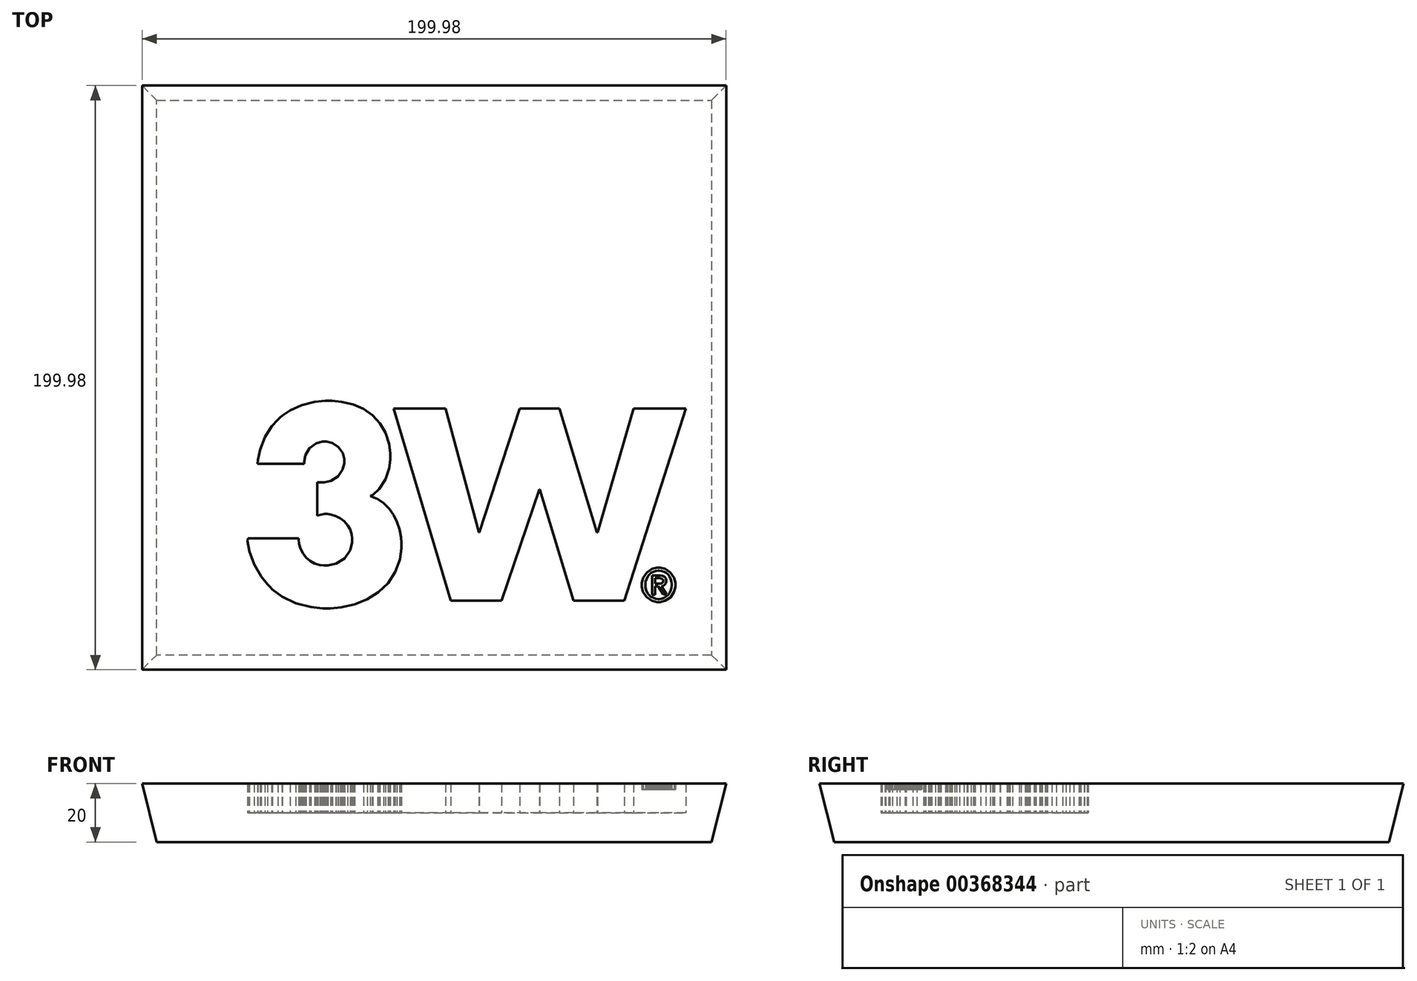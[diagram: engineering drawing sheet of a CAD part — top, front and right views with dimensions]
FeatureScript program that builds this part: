
annotation { "Feature Type Name" : "Feature", "Feature Type Description" : "" }
export const myFeature = defineFeature(function(context is Context, id is Id, definition is map)
    precondition{}
    {
        {
            var Q0;
            Q0=qCreatedBy(makeId("Top.planeOp"),FACE);
            var sketch = newSketch(context, id + "F0", { "sketchPlane" : qUnion([Q0])});
            skLineSegment(sketch, "E0", {"start": v(-100, 100) * mm, "end": v(100, 100) * mm});
            skLineSegment(sketch, "E1", {"start": v(100, 100) * mm, "end": v(100, -100) * mm});
            skLineSegment(sketch, "E2", {"start": v(100, -100) * mm, "end": v(-100, -100) * mm});
            skLineSegment(sketch, "E3", {"start": v(-100, -100) * mm, "end": v(-100, 100) * mm});
            skLineSegment(sketch, "E4", {"start": v(76.92, -70.57) * mm, "end": v(77.07, -70.57) * mm});
            skLineSegment(sketch, "E5", {"start": v(77.07, -70.57) * mm, "end": v(77.5, -70.55) * mm});
            skLineSegment(sketch, "E6", {"start": v(77.5, -70.55) * mm, "end": v(77.99, -70.42) * mm});
            skLineSegment(sketch, "E7", {"start": v(77.99, -70.42) * mm, "end": v(78.32, -70.11) * mm});
            skLineSegment(sketch, "E8", {"start": v(78.32, -70.11) * mm, "end": v(78.44, -69.69) * mm});
            skLineSegment(sketch, "E9", {"start": v(78.44, -69.69) * mm, "end": v(78.44, -69.55) * mm});
            skLineSegment(sketch, "E10", {"start": v(78.44, -69.55) * mm, "end": v(78.44, -69.43) * mm});
            skLineSegment(sketch, "E11", {"start": v(78.44, -69.43) * mm, "end": v(78.3, -69.08) * mm});
            skLineSegment(sketch, "E12", {"start": v(78.3, -69.08) * mm, "end": v(77.97, -68.82) * mm});
            skLineSegment(sketch, "E13", {"start": v(77.97, -68.82) * mm, "end": v(77.52, -68.7) * mm});
            skLineSegment(sketch, "E14", {"start": v(77.52, -68.7) * mm, "end": v(77.15, -68.67) * mm});
            skLineSegment(sketch, "E15", {"start": v(77.15, -68.67) * mm, "end": v(77.03, -68.67) * mm});
            skLineSegment(sketch, "E16", {"start": v(77.03, -68.67) * mm, "end": v(75.72, -68.67) * mm});
            skLineSegment(sketch, "E17", {"start": v(75.72, -68.67) * mm, "end": v(75.72, -70.57) * mm});
            skLineSegment(sketch, "E18", {"start": v(75.72, -70.57) * mm, "end": v(76.92, -70.57) * mm});
            skLineSegment(sketch, "E19", {"start": v(75.72, -74.28) * mm, "end": v(74.67, -74.28) * mm});
            skLineSegment(sketch, "E20", {"start": v(74.67, -74.28) * mm, "end": v(74.67, -67.75) * mm});
            skLineSegment(sketch, "E21", {"start": v(74.67, -67.75) * mm, "end": v(77.14, -67.75) * mm});
            skLineSegment(sketch, "E22", {"start": v(77.14, -67.75) * mm, "end": v(77.4, -67.75) * mm});
            skLineSegment(sketch, "E23", {"start": v(77.4, -67.75) * mm, "end": v(78.17, -67.86) * mm});
            skLineSegment(sketch, "E24", {"start": v(78.17, -67.86) * mm, "end": v(78.91, -68.2) * mm});
            skLineSegment(sketch, "E25", {"start": v(78.91, -68.2) * mm, "end": v(79.35, -68.78) * mm});
            skLineSegment(sketch, "E26", {"start": v(79.35, -68.78) * mm, "end": v(79.5, -69.4) * mm});
            skLineSegment(sketch, "E27", {"start": v(79.5, -69.4) * mm, "end": v(79.5, -69.62) * mm});
            skLineSegment(sketch, "E28", {"start": v(79.5, -69.62) * mm, "end": v(79.5, -69.8) * mm});
            skLineSegment(sketch, "E29", {"start": v(79.5, -69.8) * mm, "end": v(79.37, -70.37) * mm});
            skLineSegment(sketch, "E30", {"start": v(79.37, -70.37) * mm, "end": v(79, -70.9) * mm});
            skLineSegment(sketch, "E31", {"start": v(79, -70.9) * mm, "end": v(78.47, -71.23) * mm});
            skLineSegment(sketch, "E32", {"start": v(78.47, -71.23) * mm, "end": v(77.97, -71.36) * mm});
            skLineSegment(sketch, "E33", {"start": v(77.97, -71.36) * mm, "end": v(77.8, -71.38) * mm});
            skLineSegment(sketch, "E34", {"start": v(77.8, -71.38) * mm, "end": v(79.64, -74.24) * mm});
            skLineSegment(sketch, "E35", {"start": v(79.64, -74.24) * mm, "end": v(78.44, -74.24) * mm});
            skLineSegment(sketch, "E36", {"start": v(78.44, -74.24) * mm, "end": v(76.75, -71.46) * mm});
            skLineSegment(sketch, "E37", {"start": v(76.75, -71.46) * mm, "end": v(75.72, -71.46) * mm});
            skLineSegment(sketch, "E38", {"start": v(75.72, -71.46) * mm, "end": v(75.72, -74.28) * mm});
            skLineSegment(sketch, "E39", {"start": v(76.89, -66.06) * mm, "end": v(76.66, -66.06) * mm});
            skLineSegment(sketch, "E40", {"start": v(76.66, -66.06) * mm, "end": v(75.96, -66.15) * mm});
            skLineSegment(sketch, "E41", {"start": v(75.96, -66.15) * mm, "end": v(75.1, -66.42) * mm});
            skLineSegment(sketch, "E42", {"start": v(75.1, -66.42) * mm, "end": v(74.33, -66.84) * mm});
            skLineSegment(sketch, "E43", {"start": v(74.33, -66.84) * mm, "end": v(73.66, -67.42) * mm});
            skLineSegment(sketch, "E44", {"start": v(73.66, -67.42) * mm, "end": v(73.1, -68.13) * mm});
            skLineSegment(sketch, "E45", {"start": v(73.1, -68.13) * mm, "end": v(72.7, -68.96) * mm});
            skLineSegment(sketch, "E46", {"start": v(72.7, -68.96) * mm, "end": v(72.43, -69.9) * mm});
            skLineSegment(sketch, "E47", {"start": v(72.43, -69.9) * mm, "end": v(72.34, -70.67) * mm});
            skLineSegment(sketch, "E48", {"start": v(72.34, -70.67) * mm, "end": v(72.34, -70.93) * mm});
            skLineSegment(sketch, "E49", {"start": v(72.34, -70.93) * mm, "end": v(72.34, -71.17) * mm});
            skLineSegment(sketch, "E50", {"start": v(72.34, -71.17) * mm, "end": v(72.42, -71.9) * mm});
            skLineSegment(sketch, "E51", {"start": v(72.42, -71.9) * mm, "end": v(72.65, -72.82) * mm});
            skLineSegment(sketch, "E52", {"start": v(72.65, -72.82) * mm, "end": v(73.03, -73.64) * mm});
            skLineSegment(sketch, "E53", {"start": v(73.03, -73.64) * mm, "end": v(73.55, -74.36) * mm});
            skLineSegment(sketch, "E54", {"start": v(73.55, -74.36) * mm, "end": v(74.2, -74.96) * mm});
            skLineSegment(sketch, "E55", {"start": v(74.2, -74.96) * mm, "end": v(74.99, -75.4) * mm});
            skLineSegment(sketch, "E56", {"start": v(74.99, -75.4) * mm, "end": v(75.88, -75.7) * mm});
            skLineSegment(sketch, "E57", {"start": v(75.88, -75.7) * mm, "end": v(76.64, -75.8) * mm});
            skLineSegment(sketch, "E58", {"start": v(76.64, -75.8) * mm, "end": v(76.89, -75.8) * mm});
            skLineSegment(sketch, "E59", {"start": v(76.89, -75.8) * mm, "end": v(77.12, -75.8) * mm});
            skLineSegment(sketch, "E60", {"start": v(77.12, -75.8) * mm, "end": v(77.8, -75.7) * mm});
            skLineSegment(sketch, "E61", {"start": v(77.8, -75.7) * mm, "end": v(78.65, -75.44) * mm});
            skLineSegment(sketch, "E62", {"start": v(78.65, -75.44) * mm, "end": v(79.42, -75.01) * mm});
            skLineSegment(sketch, "E63", {"start": v(79.42, -75.01) * mm, "end": v(80.08, -74.44) * mm});
            skLineSegment(sketch, "E64", {"start": v(80.08, -74.44) * mm, "end": v(80.63, -73.74) * mm});
            skLineSegment(sketch, "E65", {"start": v(80.63, -73.74) * mm, "end": v(81.05, -72.9) * mm});
            skLineSegment(sketch, "E66", {"start": v(81.05, -72.9) * mm, "end": v(81.31, -71.97) * mm});
            skLineSegment(sketch, "E67", {"start": v(81.31, -71.97) * mm, "end": v(81.4, -71.19) * mm});
            skLineSegment(sketch, "E68", {"start": v(81.4, -71.19) * mm, "end": v(81.4, -70.93) * mm});
            skLineSegment(sketch, "E69", {"start": v(81.4, -70.93) * mm, "end": v(81.4, -70.67) * mm});
            skLineSegment(sketch, "E70", {"start": v(81.4, -70.67) * mm, "end": v(81.31, -69.89) * mm});
            skLineSegment(sketch, "E71", {"start": v(81.31, -69.89) * mm, "end": v(81.05, -68.94) * mm});
            skLineSegment(sketch, "E72", {"start": v(81.05, -68.94) * mm, "end": v(80.64, -68.11) * mm});
            skLineSegment(sketch, "E73", {"start": v(80.64, -68.11) * mm, "end": v(80.1, -67.4) * mm});
            skLineSegment(sketch, "E74", {"start": v(80.1, -67.4) * mm, "end": v(79.43, -66.83) * mm});
            skLineSegment(sketch, "E75", {"start": v(79.43, -66.83) * mm, "end": v(78.66, -66.41) * mm});
            skLineSegment(sketch, "E76", {"start": v(78.66, -66.41) * mm, "end": v(77.81, -66.15) * mm});
            skLineSegment(sketch, "E77", {"start": v(77.81, -66.15) * mm, "end": v(77.12, -66.06) * mm});
            skLineSegment(sketch, "E78", {"start": v(77.12, -66.06) * mm, "end": v(76.89, -66.06) * mm});
            skLineSegment(sketch, "E79", {"start": v(76.89, -76.82) * mm, "end": v(76.3, -76.82) * mm});
            skLineSegment(sketch, "E80", {"start": v(76.3, -76.82) * mm, "end": v(74.55, -76.37) * mm});
            skLineSegment(sketch, "E81", {"start": v(74.55, -76.37) * mm, "end": v(72.72, -75.13) * mm});
            skLineSegment(sketch, "E82", {"start": v(72.72, -75.13) * mm, "end": v(71.53, -73.26) * mm});
            skLineSegment(sketch, "E83", {"start": v(71.53, -73.26) * mm, "end": v(71.1, -71.5) * mm});
            skLineSegment(sketch, "E84", {"start": v(71.1, -71.5) * mm, "end": v(71.1, -70.93) * mm});
            skLineSegment(sketch, "E85", {"start": v(71.1, -70.93) * mm, "end": v(71.1, -70.32) * mm});
            skLineSegment(sketch, "E86", {"start": v(71.1, -70.32) * mm, "end": v(71.57, -68.52) * mm});
            skLineSegment(sketch, "E87", {"start": v(71.57, -68.52) * mm, "end": v(72.83, -66.66) * mm});
            skLineSegment(sketch, "E88", {"start": v(72.83, -66.66) * mm, "end": v(74.67, -65.46) * mm});
            skLineSegment(sketch, "E89", {"start": v(74.67, -65.46) * mm, "end": v(76.33, -65.03) * mm});
            skLineSegment(sketch, "E90", {"start": v(76.33, -65.03) * mm, "end": v(76.89, -65.03) * mm});
            skLineSegment(sketch, "E91", {"start": v(76.89, -65.03) * mm, "end": v(77.44, -65.03) * mm});
            skLineSegment(sketch, "E92", {"start": v(77.44, -65.03) * mm, "end": v(79.1, -65.46) * mm});
            skLineSegment(sketch, "E93", {"start": v(79.1, -65.46) * mm, "end": v(80.93, -66.66) * mm});
            skLineSegment(sketch, "E94", {"start": v(80.93, -66.66) * mm, "end": v(82.18, -68.52) * mm});
            skLineSegment(sketch, "E95", {"start": v(82.18, -68.52) * mm, "end": v(82.64, -70.32) * mm});
            skLineSegment(sketch, "E96", {"start": v(82.64, -70.32) * mm, "end": v(82.64, -70.93) * mm});
            skLineSegment(sketch, "E97", {"start": v(82.64, -70.93) * mm, "end": v(82.64, -71.53) * mm});
            skLineSegment(sketch, "E98", {"start": v(82.64, -71.53) * mm, "end": v(82.2, -73.33) * mm});
            skLineSegment(sketch, "E99", {"start": v(82.2, -73.33) * mm, "end": v(80.94, -75.2) * mm});
            skLineSegment(sketch, "E100", {"start": v(80.94, -75.2) * mm, "end": v(79.1, -76.4) * mm});
            skLineSegment(sketch, "E101", {"start": v(79.1, -76.4) * mm, "end": v(77.44, -76.82) * mm});
            skLineSegment(sketch, "E102", {"start": v(77.44, -76.82) * mm, "end": v(76.89, -76.82) * mm});
            skLineSegment(sketch, "E103", {"start": v(-60.45, -29.5) * mm, "end": v(-60.32, -28.28) * mm});
            skLineSegment(sketch, "E104", {"start": v(-60.32, -28.28) * mm, "end": v(-59.54, -24.65) * mm});
            skLineSegment(sketch, "E105", {"start": v(-59.54, -24.65) * mm, "end": v(-57.91, -20.4) * mm});
            skLineSegment(sketch, "E106", {"start": v(-57.91, -20.4) * mm, "end": v(-55.63, -16.72) * mm});
            skLineSegment(sketch, "E107", {"start": v(-55.63, -16.72) * mm, "end": v(-53.54, -14.33) * mm});
            skLineSegment(sketch, "E108", {"start": v(-53.54, -14.33) * mm, "end": v(-52.76, -13.63) * mm});
            skLineSegment(sketch, "E109", {"start": v(-52.76, -13.63) * mm, "end": v(-51.97, -12.93) * mm});
            skLineSegment(sketch, "E110", {"start": v(-51.97, -12.93) * mm, "end": v(-49.32, -11.17) * mm});
            skLineSegment(sketch, "E111", {"start": v(-49.32, -11.17) * mm, "end": v(-45.33, -9.4) * mm});
            skLineSegment(sketch, "E112", {"start": v(-45.33, -9.4) * mm, "end": v(-40.87, -8.32) * mm});
            skLineSegment(sketch, "E113", {"start": v(-40.87, -8.32) * mm, "end": v(-37.22, -7.96) * mm});
            skLineSegment(sketch, "E114", {"start": v(-37.22, -7.96) * mm, "end": v(-36, -7.96) * mm});
            skLineSegment(sketch, "E115", {"start": v(-36, -7.96) * mm, "end": v(-34.93, -7.96) * mm});
            skLineSegment(sketch, "E116", {"start": v(-34.93, -7.96) * mm, "end": v(-31.72, -8.27) * mm});
            skLineSegment(sketch, "E117", {"start": v(-31.72, -8.27) * mm, "end": v(-27.75, -9.21) * mm});
            skLineSegment(sketch, "E118", {"start": v(-27.75, -9.21) * mm, "end": v(-24.17, -10.76) * mm});
            skLineSegment(sketch, "E119", {"start": v(-24.17, -10.76) * mm, "end": v(-21.07, -12.9) * mm});
            skLineSegment(sketch, "E120", {"start": v(-21.07, -12.9) * mm, "end": v(-18.52, -15.61) * mm});
            skLineSegment(sketch, "E121", {"start": v(-18.52, -15.61) * mm, "end": v(-16.6, -18.9) * mm});
            skLineSegment(sketch, "E122", {"start": v(-16.6, -18.9) * mm, "end": v(-15.4, -22.72) * mm});
            skLineSegment(sketch, "E123", {"start": v(-15.4, -22.72) * mm, "end": v(-14.98, -25.99) * mm});
            skLineSegment(sketch, "E124", {"start": v(-14.98, -25.99) * mm, "end": v(-14.98, -27.08) * mm});
            skLineSegment(sketch, "E125", {"start": v(-14.98, -27.08) * mm, "end": v(-14.98, -28.06) * mm});
            skLineSegment(sketch, "E126", {"start": v(-14.98, -28.06) * mm, "end": v(-15.38, -31.01) * mm});
            skLineSegment(sketch, "E127", {"start": v(-15.38, -31.01) * mm, "end": v(-16.62, -34.78) * mm});
            skLineSegment(sketch, "E128", {"start": v(-16.62, -34.78) * mm, "end": v(-18.76, -38.08) * mm});
            skLineSegment(sketch, "E129", {"start": v(-18.76, -38.08) * mm, "end": v(-21, -40.1) * mm});
            skLineSegment(sketch, "E130", {"start": v(-21, -40.1) * mm, "end": v(-21.85, -40.59) * mm});
            skLineSegment(sketch, "E131", {"start": v(-21.85, -40.59) * mm, "end": v(-21.22, -40.75) * mm});
            skLineSegment(sketch, "E132", {"start": v(-21.22, -40.75) * mm, "end": v(-19.39, -41.55) * mm});
            skLineSegment(sketch, "E133", {"start": v(-19.39, -41.55) * mm, "end": v(-17.23, -43) * mm});
            skLineSegment(sketch, "E134", {"start": v(-17.23, -43) * mm, "end": v(-15.4, -44.86) * mm});
            skLineSegment(sketch, "E135", {"start": v(-15.4, -44.86) * mm, "end": v(-13.87, -47.04) * mm});
            skLineSegment(sketch, "E136", {"start": v(-13.87, -47.04) * mm, "end": v(-12.68, -49.44) * mm});
            skLineSegment(sketch, "E137", {"start": v(-12.68, -49.44) * mm, "end": v(-11.82, -52) * mm});
            skLineSegment(sketch, "E138", {"start": v(-11.82, -52) * mm, "end": v(-11.3, -54.6) * mm});
            skLineSegment(sketch, "E139", {"start": v(-11.3, -54.6) * mm, "end": v(-11.13, -56.52) * mm});
            skLineSegment(sketch, "E140", {"start": v(-11.13, -56.52) * mm, "end": v(-11.13, -57.17) * mm});
            skLineSegment(sketch, "E141", {"start": v(-11.13, -57.17) * mm, "end": v(-11.13, -58.43) * mm});
            skLineSegment(sketch, "E142", {"start": v(-11.13, -58.43) * mm, "end": v(-11.7, -62.24) * mm});
            skLineSegment(sketch, "E143", {"start": v(-11.7, -62.24) * mm, "end": v(-13.29, -66.64) * mm});
            skLineSegment(sketch, "E144", {"start": v(-13.29, -66.64) * mm, "end": v(-15.77, -70.4) * mm});
            skLineSegment(sketch, "E145", {"start": v(-15.77, -70.4) * mm, "end": v(-19.01, -73.46) * mm});
            skLineSegment(sketch, "E146", {"start": v(-19.01, -73.46) * mm, "end": v(-22.86, -75.87) * mm});
            skLineSegment(sketch, "E147", {"start": v(-22.86, -75.87) * mm, "end": v(-27.19, -77.58) * mm});
            skLineSegment(sketch, "E148", {"start": v(-27.19, -77.58) * mm, "end": v(-31.85, -78.62) * mm});
            skLineSegment(sketch, "E149", {"start": v(-31.85, -78.62) * mm, "end": v(-35.5, -78.97) * mm});
            skLineSegment(sketch, "E150", {"start": v(-35.5, -78.97) * mm, "end": v(-36.7, -78.97) * mm});
            skLineSegment(sketch, "E151", {"start": v(-36.7, -78.97) * mm, "end": v(-38.08, -78.97) * mm});
            skLineSegment(sketch, "E152", {"start": v(-38.08, -78.97) * mm, "end": v(-42.2, -78.57) * mm});
            skLineSegment(sketch, "E153", {"start": v(-42.2, -78.57) * mm, "end": v(-47.35, -77.29) * mm});
            skLineSegment(sketch, "E154", {"start": v(-47.35, -77.29) * mm, "end": v(-52.08, -75) * mm});
            skLineSegment(sketch, "E155", {"start": v(-52.08, -75) * mm, "end": v(-55.37, -72.53) * mm});
            skLineSegment(sketch, "E156", {"start": v(-55.37, -72.53) * mm, "end": v(-56.32, -71.56) * mm});
            skLineSegment(sketch, "E157", {"start": v(-56.32, -71.56) * mm, "end": v(-57.1, -70.76) * mm});
            skLineSegment(sketch, "E158", {"start": v(-57.1, -70.76) * mm, "end": v(-59.17, -68.08) * mm});
            skLineSegment(sketch, "E159", {"start": v(-59.17, -68.08) * mm, "end": v(-61.61, -63.92) * mm});
            skLineSegment(sketch, "E160", {"start": v(-61.61, -63.92) * mm, "end": v(-63.29, -59.43) * mm});
            skLineSegment(sketch, "E161", {"start": v(-63.29, -59.43) * mm, "end": v(-63.87, -56.09) * mm});
            skLineSegment(sketch, "E162", {"start": v(-63.87, -56.09) * mm, "end": v(-63.83, -54.98) * mm});
            skLineSegment(sketch, "E163", {"start": v(-63.83, -54.98) * mm, "end": v(-46.37, -54.98) * mm});
            skLineSegment(sketch, "E164", {"start": v(-46.37, -54.98) * mm, "end": v(-46.37, -55.45) * mm});
            skLineSegment(sketch, "E165", {"start": v(-46.37, -55.45) * mm, "end": v(-46.2, -56.88) * mm});
            skLineSegment(sketch, "E166", {"start": v(-46.2, -56.88) * mm, "end": v(-45.7, -58.64) * mm});
            skLineSegment(sketch, "E167", {"start": v(-45.7, -58.64) * mm, "end": v(-44.9, -60.23) * mm});
            skLineSegment(sketch, "E168", {"start": v(-44.9, -60.23) * mm, "end": v(-43.82, -61.61) * mm});
            skLineSegment(sketch, "E169", {"start": v(-43.82, -61.61) * mm, "end": v(-42.5, -62.75) * mm});
            skLineSegment(sketch, "E170", {"start": v(-42.5, -62.75) * mm, "end": v(-40.93, -63.6) * mm});
            skLineSegment(sketch, "E171", {"start": v(-40.93, -63.6) * mm, "end": v(-39.15, -64.14) * mm});
            skLineSegment(sketch, "E172", {"start": v(-39.15, -64.14) * mm, "end": v(-37.69, -64.33) * mm});
            skLineSegment(sketch, "E173", {"start": v(-37.69, -64.33) * mm, "end": v(-37.2, -64.33) * mm});
            skLineSegment(sketch, "E174", {"start": v(-37.2, -64.33) * mm, "end": v(-36.3, -64.33) * mm});
            skLineSegment(sketch, "E175", {"start": v(-36.3, -64.33) * mm, "end": v(-33.56, -63.7) * mm});
            skLineSegment(sketch, "E176", {"start": v(-33.56, -63.7) * mm, "end": v(-30.66, -61.92) * mm});
            skLineSegment(sketch, "E177", {"start": v(-30.66, -61.92) * mm, "end": v(-28.73, -59.13) * mm});
            skLineSegment(sketch, "E178", {"start": v(-28.73, -59.13) * mm, "end": v(-28.03, -56.41) * mm});
            skLineSegment(sketch, "E179", {"start": v(-28.03, -56.41) * mm, "end": v(-28.03, -55.5) * mm});
            skLineSegment(sketch, "E180", {"start": v(-28.03, -55.5) * mm, "end": v(-28.03, -55.06) * mm});
            skLineSegment(sketch, "E181", {"start": v(-28.03, -55.06) * mm, "end": v(-28.22, -53.7) * mm});
            skLineSegment(sketch, "E182", {"start": v(-28.22, -53.7) * mm, "end": v(-28.77, -52.03) * mm});
            skLineSegment(sketch, "E183", {"start": v(-28.77, -52.03) * mm, "end": v(-29.63, -50.53) * mm});
            skLineSegment(sketch, "E184", {"start": v(-29.63, -50.53) * mm, "end": v(-30.76, -49.23) * mm});
            skLineSegment(sketch, "E185", {"start": v(-30.76, -49.23) * mm, "end": v(-32.12, -48.17) * mm});
            skLineSegment(sketch, "E186", {"start": v(-32.12, -48.17) * mm, "end": v(-33.65, -47.37) * mm});
            skLineSegment(sketch, "E187", {"start": v(-33.65, -47.37) * mm, "end": v(-35.33, -46.86) * mm});
            skLineSegment(sketch, "E188", {"start": v(-35.33, -46.86) * mm, "end": v(-36.65, -46.69) * mm});
            skLineSegment(sketch, "E189", {"start": v(-36.65, -46.69) * mm, "end": v(-37.1, -46.69) * mm});
            skLineSegment(sketch, "E190", {"start": v(-37.1, -46.69) * mm, "end": v(-37.47, -46.69) * mm});
            skLineSegment(sketch, "E191", {"start": v(-37.47, -46.69) * mm, "end": v(-38.62, -46.85) * mm});
            skLineSegment(sketch, "E192", {"start": v(-38.62, -46.85) * mm, "end": v(-39.82, -47.15) * mm});
            skLineSegment(sketch, "E193", {"start": v(-39.82, -47.15) * mm, "end": v(-40.06, -47.22) * mm});
            skLineSegment(sketch, "E194", {"start": v(-40.06, -47.22) * mm, "end": v(-40.06, -35.79) * mm});
            skLineSegment(sketch, "E195", {"start": v(-40.06, -35.79) * mm, "end": v(-38.33, -35.79) * mm});
            skLineSegment(sketch, "E196", {"start": v(-38.33, -35.79) * mm, "end": v(-37.57, -35.79) * mm});
            skLineSegment(sketch, "E197", {"start": v(-37.57, -35.79) * mm, "end": v(-35.3, -35.3) * mm});
            skLineSegment(sketch, "E198", {"start": v(-35.3, -35.3) * mm, "end": v(-32.93, -33.87) * mm});
            skLineSegment(sketch, "E199", {"start": v(-32.93, -33.87) * mm, "end": v(-31.37, -31.6) * mm});
            skLineSegment(sketch, "E200", {"start": v(-31.37, -31.6) * mm, "end": v(-30.81, -29.31) * mm});
            skLineSegment(sketch, "E201", {"start": v(-30.81, -29.31) * mm, "end": v(-30.81, -28.56) * mm});
            skLineSegment(sketch, "E202", {"start": v(-30.81, -28.56) * mm, "end": v(-30.81, -27.87) * mm});
            skLineSegment(sketch, "E203", {"start": v(-30.81, -27.87) * mm, "end": v(-31.33, -25.82) * mm});
            skLineSegment(sketch, "E204", {"start": v(-31.33, -25.82) * mm, "end": v(-32.74, -23.73) * mm});
            skLineSegment(sketch, "E205", {"start": v(-32.74, -23.73) * mm, "end": v(-34.86, -22.4) * mm});
            skLineSegment(sketch, "E206", {"start": v(-34.86, -22.4) * mm, "end": v(-36.85, -21.92) * mm});
            skLineSegment(sketch, "E207", {"start": v(-36.85, -21.92) * mm, "end": v(-37.52, -21.92) * mm});
            skLineSegment(sketch, "E208", {"start": v(-37.52, -21.92) * mm, "end": v(-38.25, -21.92) * mm});
            skLineSegment(sketch, "E209", {"start": v(-38.25, -21.92) * mm, "end": v(-40.46, -22.5) * mm});
            skLineSegment(sketch, "E210", {"start": v(-40.46, -22.5) * mm, "end": v(-42.68, -24.12) * mm});
            skLineSegment(sketch, "E211", {"start": v(-42.68, -24.12) * mm, "end": v(-44.06, -26.52) * mm});
            skLineSegment(sketch, "E212", {"start": v(-44.06, -26.52) * mm, "end": v(-44.51, -28.76) * mm});
            skLineSegment(sketch, "E213", {"start": v(-44.51, -28.76) * mm, "end": v(-44.5, -29.5) * mm});
            skLineSegment(sketch, "E214", {"start": v(-44.5, -29.5) * mm, "end": v(-60.45, -29.5) * mm});
            skLineSegment(sketch, "E215", {"start": v(15.33, -53.04) * mm, "end": v(15.5, -53.04) * mm});
            skLineSegment(sketch, "E216", {"start": v(15.5, -53.04) * mm, "end": v(29.3, -10.57) * mm});
            skLineSegment(sketch, "E217", {"start": v(29.3, -10.57) * mm, "end": v(42.88, -10.57) * mm});
            skLineSegment(sketch, "E218", {"start": v(42.88, -10.57) * mm, "end": v(55.8, -53.04) * mm});
            skLineSegment(sketch, "E219", {"start": v(55.8, -53.04) * mm, "end": v(55.97, -53.04) * mm});
            skLineSegment(sketch, "E220", {"start": v(55.97, -53.04) * mm, "end": v(68.35, -10.57) * mm});
            skLineSegment(sketch, "E221", {"start": v(68.35, -10.57) * mm, "end": v(86.17, -10.57) * mm});
            skLineSegment(sketch, "E222", {"start": v(86.17, -10.57) * mm, "end": v(65.14, -76.36) * mm});
            skLineSegment(sketch, "E223", {"start": v(65.14, -76.36) * mm, "end": v(47.68, -76.36) * mm});
            skLineSegment(sketch, "E224", {"start": v(47.68, -76.36) * mm, "end": v(36.18, -38.22) * mm});
            skLineSegment(sketch, "E225", {"start": v(36.18, -38.22) * mm, "end": v(36, -38.22) * mm});
            skLineSegment(sketch, "E226", {"start": v(36, -38.22) * mm, "end": v(23.09, -76.36) * mm});
            skLineSegment(sketch, "E227", {"start": v(23.09, -76.36) * mm, "end": v(5.73, -76.36) * mm});
            skLineSegment(sketch, "E228", {"start": v(5.73, -76.36) * mm, "end": v(-13.92, -10.57) * mm});
            skLineSegment(sketch, "E229", {"start": v(-13.92, -10.57) * mm, "end": v(3.9, -10.57) * mm});
            skLineSegment(sketch, "E230", {"start": v(3.9, -10.57) * mm, "end": v(15.33, -53.04) * mm});
            skSolve(sketch);
        }
        {
            var Q0;
            {var subQ4=sQuery(id+"F0.wireOp",EDGE,"E2");Q0=makeQuery(id+"F0.imprint","IMPRINT",FACE,{"disambiguationData":[TD([[makeQuery(id+"F0.imprint","IMPRINT",EDGE,{"derivedFrom":subQ4}),-1.0]])]});}
            var Q1;
            Q1=makeQuery(id+"F0.imprint","IMPRINT",FACE,{"disambiguationData":[TD([[makeQuery(id+"F0.imprint","IMPRINT",EDGE,{"derivedFrom":sQuery(id+"F0.wireOp",EDGE,"E19")}),1.0]])]});
            var Q2;
            Q2=makeQuery(id+"F0.imprint","IMPRINT",FACE,{"disambiguationData":[TD([[makeQuery(id+"F0.imprint","IMPRINT",EDGE,{"derivedFrom":sQuery(id+"F0.wireOp",EDGE,"E4")}),1.0]])]});
            extrude(context, id + "F1", {"entities" : qUnion([Q0, Q1, Q2]), "depth" : 20 * mm});
        }
        {
            var Q0;
            Q0=makeQuery(id+"F0.imprint","IMPRINT",FACE,{"disambiguationData":[TD([[makeQuery(id+"F0.imprint","IMPRINT",EDGE,{"derivedFrom":sQuery(id+"F0.wireOp",EDGE,"E215")}),-1.0]])]});
            var Q1;
            Q1=makeQuery(id+"F0.imprint","IMPRINT",FACE,{"disambiguationData":[TD([[makeQuery(id+"F0.imprint","IMPRINT",EDGE,{"derivedFrom":sQuery(id+"F0.wireOp",EDGE,"E103")}),-1.0]])]});
            extrude(context, id + "F2", {"entities" : qUnion([Q0, Q1]), "operationType" : NewBodyOperationType.ADD, "depth" : 10 * mm});
        }
        {
            var Q0;
            Q0=makeQuery(id+"F0.imprint","IMPRINT",FACE,{"disambiguationData":[TD([[makeQuery(id+"F0.imprint","IMPRINT",EDGE,{"derivedFrom":sQuery(id+"F0.wireOp",EDGE,"E39")}),-1.0]])]});
            var Q1;
            Q1=makeQuery(id+"F0.imprint","IMPRINT",FACE,{"disambiguationData":[TD([[makeQuery(id+"F0.imprint","IMPRINT",EDGE,{"derivedFrom":sQuery(id+"F0.wireOp",EDGE,"E4")}),-1.0]])]});
            extrude(context, id + "F3", {"entities" : qUnion([Q0, Q1]), "operationType" : NewBodyOperationType.ADD, "depth" : 18 * mm});
        }
        {
            var Q0;
            Q0=makeQuery(id+"F1.opExtrude","CAP_EDGE",EDGE,{"disambiguationData":[OSD([sQuery(id+"F0.wireOp",EDGE,"E2")])],"isStart":true});
            var Q1;
            Q1=makeQuery(id+"F1.opExtrude","CAP_EDGE",EDGE,{"disambiguationData":[OSD([sQuery(id+"F0.wireOp",EDGE,"E3")])],"isStart":true});
            var Q2;
            Q2=makeQuery(id+"F1.opExtrude","CAP_EDGE",EDGE,{"disambiguationData":[OSD([sQuery(id+"F0.wireOp",EDGE,"E1")])],"isStart":true});
            var Q3;
            Q3=makeQuery(id+"F1.opExtrude","CAP_EDGE",EDGE,{"disambiguationData":[OSD([sQuery(id+"F0.wireOp",EDGE,"E0")])],"isStart":true});
            chamfer(context, id + "F4", {"entities" : qUnion([Q0, Q1, Q2, Q3]), "chamferType" : ChamferType.TWO_OFFSETS, "width1" : 5 * mm, "oppositeDirection" : false, "width2" : 20 * mm, "tangentPropagation" : true});
        }
    });
